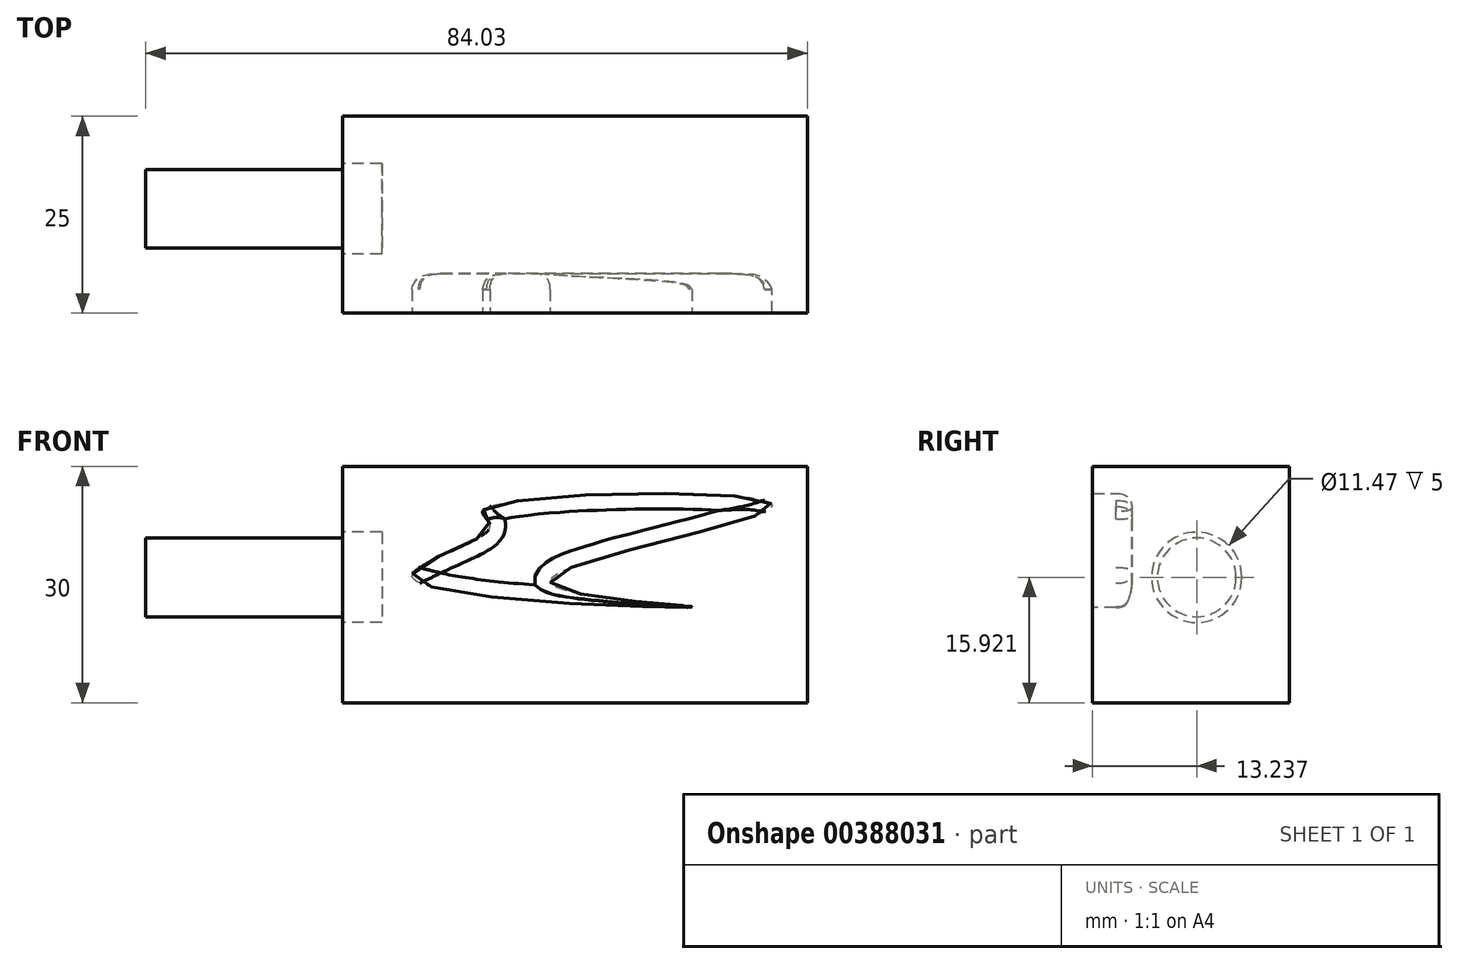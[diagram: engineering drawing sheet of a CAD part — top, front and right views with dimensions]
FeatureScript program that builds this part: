
annotation { "Feature Type Name" : "Feature", "Feature Type Description" : "" }
export const myFeature = defineFeature(function(context is Context, id is Id, definition is map)
    precondition{}
    {
        {
            var Q0;
            Q0=qCreatedBy(makeId("Front.planeOp"),FACE);
            cPlane(context, id + "F0", {"entities" : qUnion([Q0]), "cplaneType" : CPlaneType.OFFSET, "offset" : 25 * mm, "width" : 150 * mm, "height" : 150 * mm});
        }
        {
            var Q0;
            Q0=qCreatedBy(id+"F0.planeOp",FACE);
            var sketch = newSketch(context, id + "F1", { "sketchPlane" : qUnion([Q0])});
            skLineSegment(sketch, "E0.bottom", {"start": v(0, 0) * mm, "end": v(59.03, 0) * mm});
            skLineSegment(sketch, "E0.top", {"start": v(0, 30) * mm, "end": v(59.03, 30) * mm});
            skLineSegment(sketch, "E0.left", {"start": v(0, 0) * mm, "end": v(0, 30) * mm});
            skLineSegment(sketch, "E0.right", {"start": v(59.03, 0) * mm, "end": v(59.03, 30) * mm});
            skSolve(sketch);
        }
        {
            var Q0;
            Q0 = qSketchRegion(id + "F1", true);
            extrude(context, id + "F2", {"entities" : qUnion([Q0]), "depth" : 25 * mm});
        }
        {
            var Q0;
            Q0=makeQuery(id+"F2.opExtrude","CAP_FACE",FACE,{"disambiguationData":[OSD([sQuery(id+"F1.wireOp",EDGE,"E0.bottom"),sQuery(id+"F1.wireOp",EDGE,"E0.top"),sQuery(id+"F1.wireOp",EDGE,"E0.left"),sQuery(id+"F1.wireOp",EDGE,"E0.right")])],"isStart":false});
            var sketch = newSketch(context, id + "F3", { "sketchPlane" : qUnion([Q0])});
            skFitSpline(sketch, "E1", {"points": [v(17.9, 24.45) * mm, v(54.54, 25.03) * mm, v(26.38, 15.4) * mm, v(44.38, 12.17) * mm, v(8.88, 15.94) * mm, v(18.7, 22.23) * mm, v(17.9, 24.45) * mm]});
            skSolve(sketch);
        }
        {
            var Q0;
            Q0 = qSketchRegion(id + "F3", true);
            extrude(context, id + "F4", {"entities" : qUnion([Q0]), "operationType" : NewBodyOperationType.REMOVE, "oppositeDirection" : true, "depth" : 5 * mm});
        }
        {
            var Q0;
            Q0=makeQuery(id+"F4.boolean.opBoolean","COPY",FACE,{"derivedFrom":makeQuery(id+"F4.opExtrude","CAP_FACE",FACE,{"disambiguationData":[OSD([sQuery(id+"F3.wireOp",EDGE,"E1")])],"isStart":false})});
            fillet(context, id + "F5", {"entities" : qUnion([Q0]), "radius" : 2 * mm, "tangentPropagation" : true, "rho" : 0.5, "crossSection" : FilletCrossSection.CONIC, "allowEdgeOverflow" : false});
        }
        {
            var Q0;
            Q0=makeQuery(id+"F2.opExtrude","SWEPT_FACE",FACE,{"disambiguationData":[OSD([sQuery(id+"F1.wireOp",EDGE,"E0.left")])]});
            var sketch = newSketch(context, id + "F6", { "sketchPlane" : qUnion([Q0])});
            skCircle(sketch, "E2", {"center": v(36.76, 15.92) * mm, "radius": 5.74 * mm});
            skSolve(sketch);
        }
        {
            var Q0;
            Q0 = qSketchRegion(id + "F6", true);
            extrude(context, id + "F7", {"entities" : qUnion([Q0]), "operationType" : NewBodyOperationType.REMOVE, "oppositeDirection" : true, "depth" : 5 * mm});
        }
        {
            var Q0;
            Q0=makeQuery(id+"F2.opExtrude","SWEPT_FACE",FACE,{"disambiguationData":[OSD([sQuery(id+"F1.wireOp",EDGE,"E0.left")])]});
            var sketch = newSketch(context, id + "F8", { "sketchPlane" : qUnion([Q0])});
            skCircle(sketch, "E3", {"center": v(36.76, 15.92) * mm, "radius": 5 * mm});
            skSolve(sketch);
        }
        {
            var Q0;
            Q0 = qSketchRegion(id + "F8", true);
            extrude(context, id + "F9", {"entities" : qUnion([Q0]), "depth" : 25 * mm});
        }
    });
